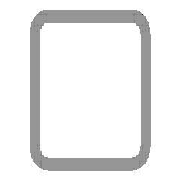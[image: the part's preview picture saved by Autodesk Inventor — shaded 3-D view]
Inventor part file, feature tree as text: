
AUTODESK INVENTOR PART (.ipt)
format: ipt  version: 2025.1 (Build 291241020, 241B)  size: 136,704 bytes
history: native  units: mm (DEFAULTED — no unit token found)
features: other x4, sketch x1, plane x1
ambient origin geometry x8: Origin, YZ Plane, XZ Plane, XY Plane, X Axis, Y Axis, Z Axis, Center Point
bodies: Solid1 (feature_tree), Body (feature_tree)
feature tree (6):
  parser-record x1  (decoder bookkeeping rows leaked as tree rows — omitted from the tree; the rows remain in map.json)
  other  "Driven Length"
  other  "Start plane"
  other  "End plane"
  sketch  "Sketch3"  dims[d3=1400.0mm d4=0.0mm d7=6.0mm d9=100.0mm d11=100.0mm d12=3.0mm d13=50.0mm d14=1450.0mm d15=50.0mm d16=50.0mm d17=90.0deg d18=1400.0mm]
  plane  "Work Plane3"
